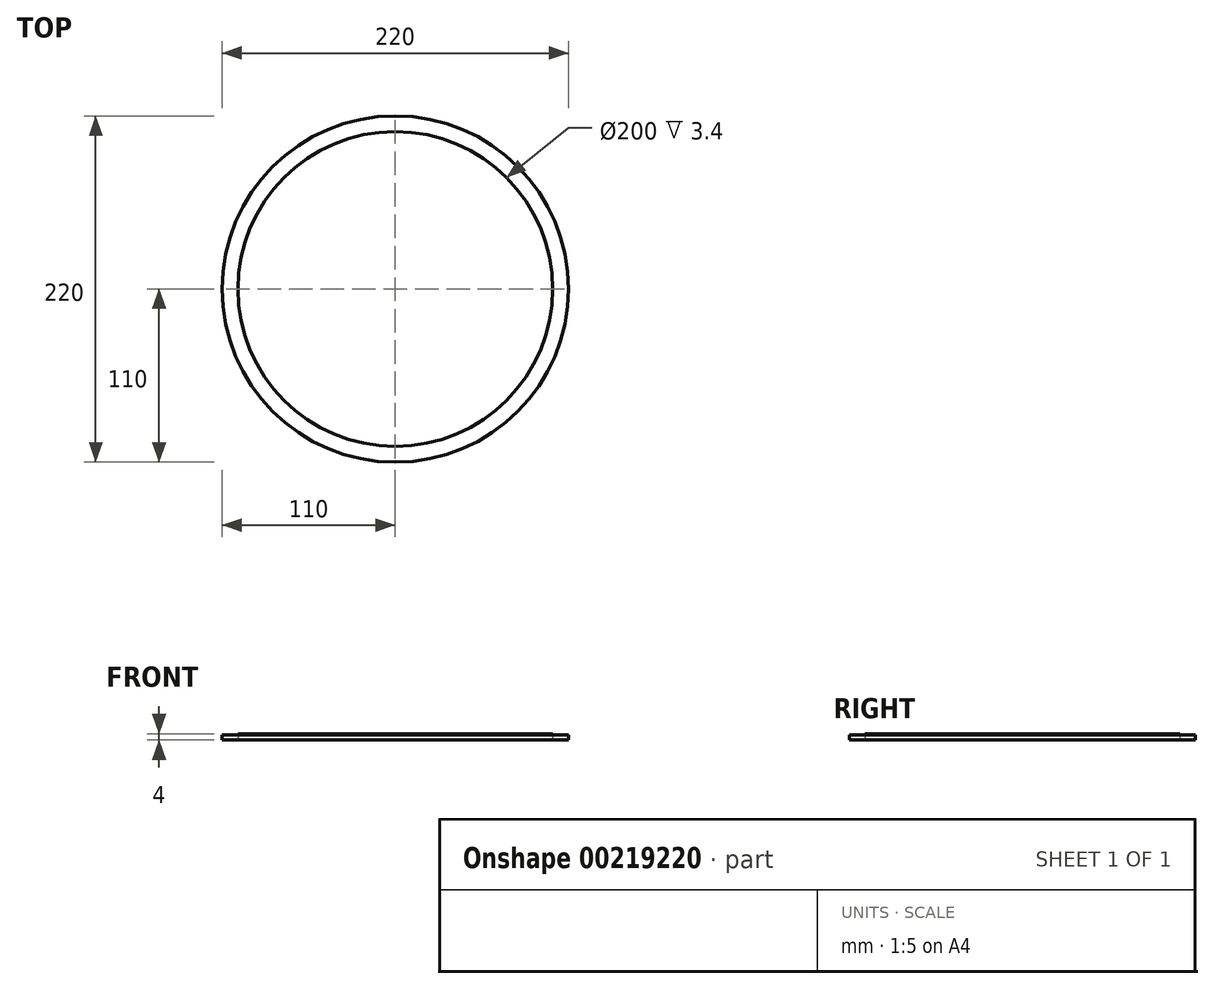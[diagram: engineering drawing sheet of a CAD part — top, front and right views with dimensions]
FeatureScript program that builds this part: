
annotation { "Feature Type Name" : "Feature", "Feature Type Description" : "" }
export const myFeature = defineFeature(function(context is Context, id is Id, definition is map)
    precondition{}
    {
        {
            assignVariable(context, id + "F0", {"name" : "plate_thk", "anyValue" : 4 * mm});
        }
        {
            assignVariable(context, id + "F1", {"name" : "rim_thk", "anyValue" : 3.4 * mm});
        }
        {
            var Q0;
            Q0=qCreatedBy(makeId("Top.planeOp"),FACE);
            var sketch = newSketch(context, id + "F2", { "sketchPlane" : qUnion([Q0])});
            skCircle(sketch, "E0", {"center": v(0, 0) * mm, "radius": 100 * mm});
            skCircle(sketch, "E1", {"center": v(0, 0) * mm, "radius": 110 * mm});
            skSolve(sketch);
        }
        {
            var Q0;
            Q0=makeQuery(id+"F2.imprint","IMPRINT",FACE,{"disambiguationData":[TD([[makeQuery(id+"F2.imprint","IMPRINT",EDGE,{"derivedFrom":sQuery(id+"F2.wireOp",EDGE,"E0")}),1.0]])]});
            extrude(context, id + "F3", {"entities" : qUnion([Q0]), "depth" : getVariable(context, 'plate_thk')});
        }
        {
            var Q0;
            Q0 = qSketchRegion(id + "F2", true);
            extrude(context, id + "F4", {"entities" : qUnion([Q0]), "depth" : getVariable(context, 'rim_thk')});
        }
    });
